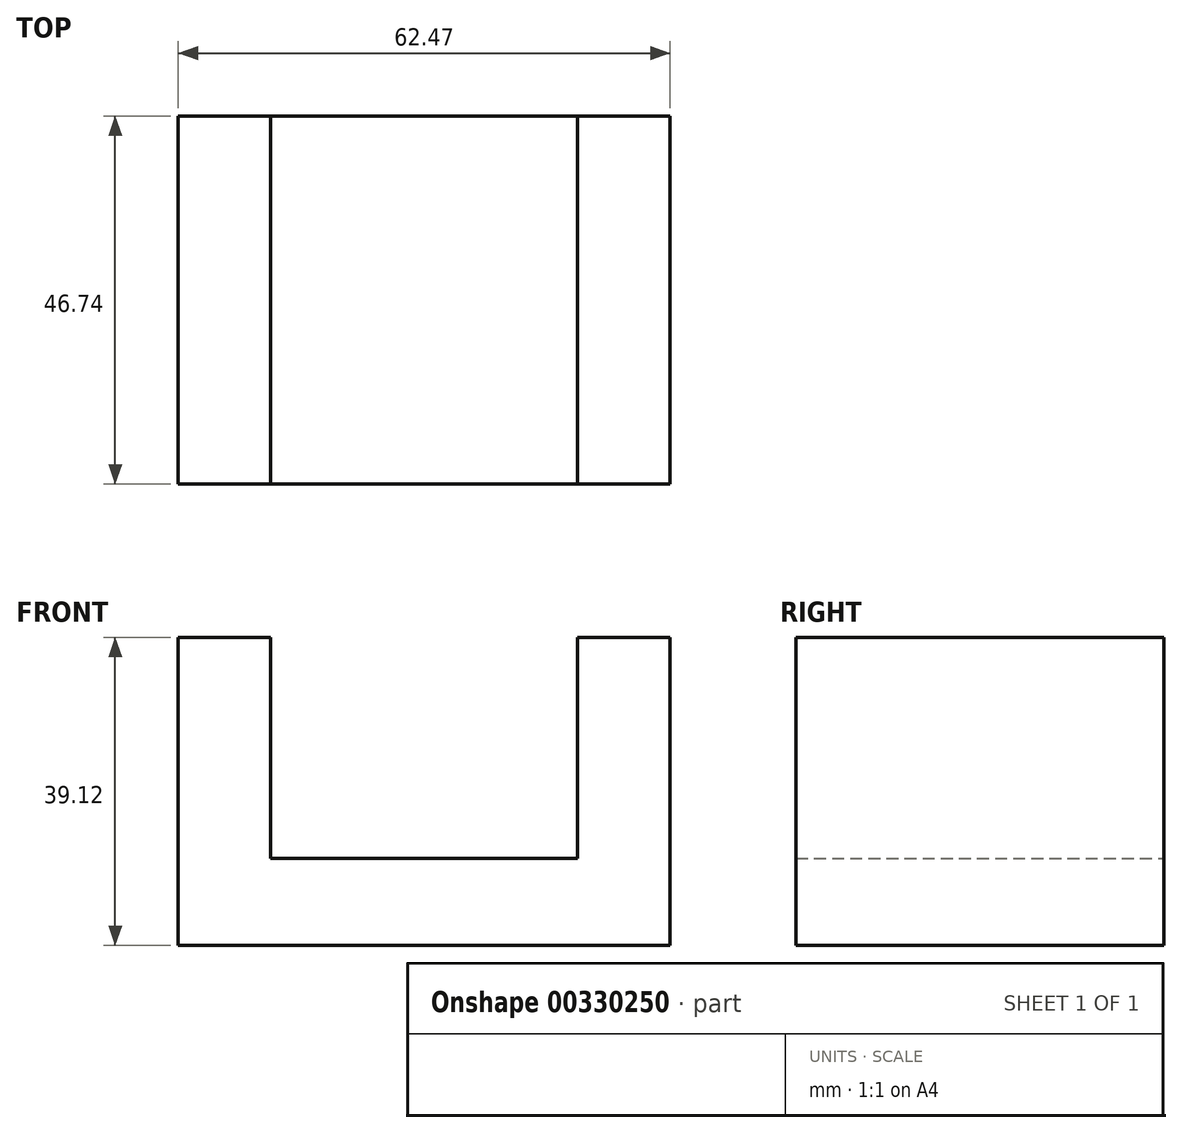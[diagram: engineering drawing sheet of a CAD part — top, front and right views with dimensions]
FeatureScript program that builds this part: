
annotation { "Feature Type Name" : "Feature", "Feature Type Description" : "" }
export const myFeature = defineFeature(function(context is Context, id is Id, definition is map)
    precondition{}
    {
        {
            var Q0;
            Q0=qCreatedBy(makeId("Front.planeOp"),FACE);
            var sketch = newSketch(context, id + "F0", { "sketchPlane" : qUnion([Q0])});
            skLineSegment(sketch, "E0.bottom", {"start": v(0, 0) * mm, "end": v(62.47, 0) * mm});
            skLineSegment(sketch, "E0.top", {"start": v(0, 39.12) * mm, "end": v(11.75, 39.12) * mm});
            skLineSegment(sketch, "E0.left", {"start": v(0, 0) * mm, "end": v(0, 39.12) * mm});
            skLineSegment(sketch, "E0.right", {"start": v(62.47, 0) * mm, "end": v(62.47, 39.12) * mm});
            skLineSegment(sketch, "E1.top", {"start": v(11.75, 11.03) * mm, "end": v(50.72, 11.03) * mm});
            skLineSegment(sketch, "E1.left", {"start": v(11.75, 39.12) * mm, "end": v(11.75, 11.03) * mm});
            skLineSegment(sketch, "E1.right", {"start": v(50.72, 39.12) * mm, "end": v(50.72, 11.03) * mm});
            skLineSegment(sketch, "E2.trimOffspring", {"start": v(50.72, 39.12) * mm, "end": v(62.47, 39.12) * mm});
            skSolve(sketch);
        }
        {
            var Q0;
            Q0=makeQuery(id+"F0.imprint","IMPRINT",FACE,{"disambiguationData":[TD([[makeQuery(id+"F0.imprint","IMPRINT",EDGE,{"derivedFrom":sQuery(id+"F0.wireOp",EDGE,"E0.bottom")}),1.0]])]});
            extrude(context, id + "F1", {"entities" : qUnion([Q0]), "depth" : 46.74 * mm});
        }
    });
